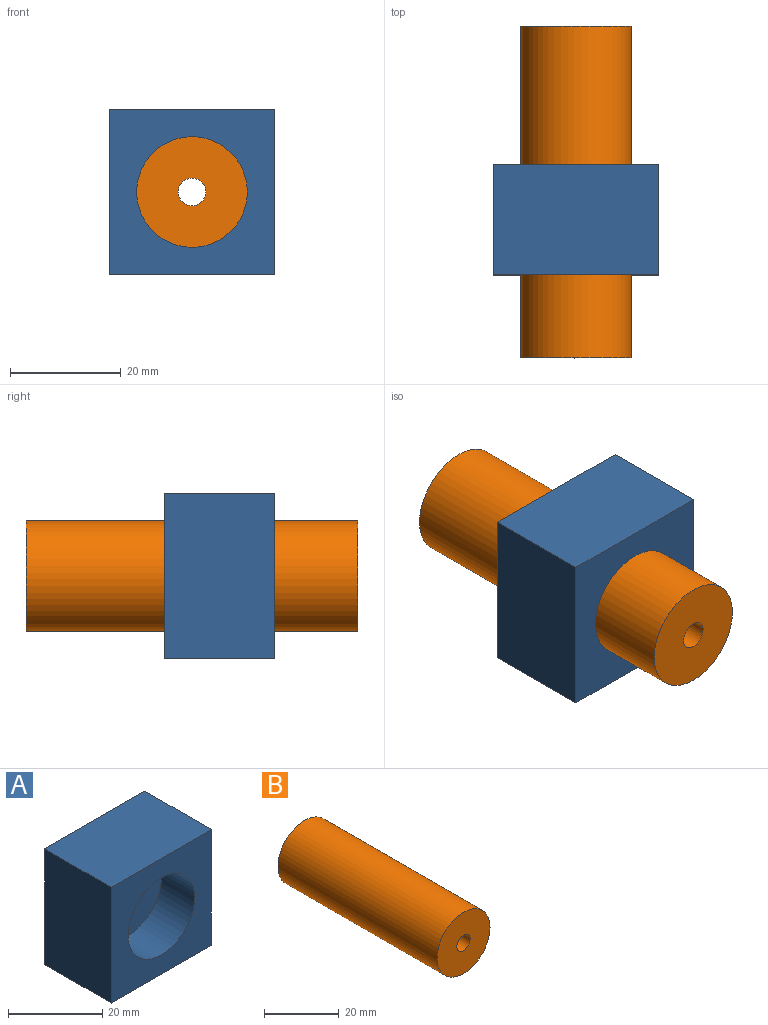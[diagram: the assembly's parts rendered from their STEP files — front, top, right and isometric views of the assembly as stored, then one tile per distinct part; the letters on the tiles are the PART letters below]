
ASSEMBLY  parts=2 mates=1
PART A: 9 faces, bbox 30x20x30 mm
  f0: plane 30x20mm, normal (0,0,-1), area 600mm2, adj f1,f3,f4,f5
  f1: plane 30x20mm, normal (1,0,0), area 600mm2, adj f0,f2,f4,f5
  f2: plane 30x20mm, normal (0,0,1), area 600mm2, adj f1,f3,f4,f5
  f3: plane 30x20mm, normal (-1,0,0), area 600mm2, adj f0,f2,f4,f5
  f4: plane 30x30mm, normal (0,-1,0), area 585.8mm2, adj f0,f1,f2,f3,f6
  f5: plane 30x30mm, normal (0,1,0), area 878.4mm2, adj f0,f1,f2,f3,f8
  f6: cylinder r=10mm len=20mm, axis (0,-1,0), area 628.3mm2, adj f4,f7
  f7: plane 20x20mm, normal (0,-1,0), area 292.5mm2, adj f6,f8
  f8: cylinder r=2.62mm len=10mm, axis (0,1,0), area 164.9mm2, adj f5,f7
PART B: 4 faces, bbox 20x60x20 mm
  f0: cylinder r=10mm len=60mm, axis (0,1,0), area 3769.9mm2, adj f1,f2
  f1: plane 20x20mm, normal (0,-1,0), area 294.5mm2, adj f0,f3
  f2: plane 20x20mm, normal (0,1,0), area 294.5mm2, adj f0,f3
  f3: cylinder r=2.5mm len=60mm, axis (0,-1,0), area 942.5mm2, adj f1,f2
PLACE A at identity fixed
PLACE B rot(axis=(1,0,0),180deg) t=(0,-25,0)mm
MATE fastened B.f0 <-> A.f6  axis (0,1,0) through (0,5,0)mm
